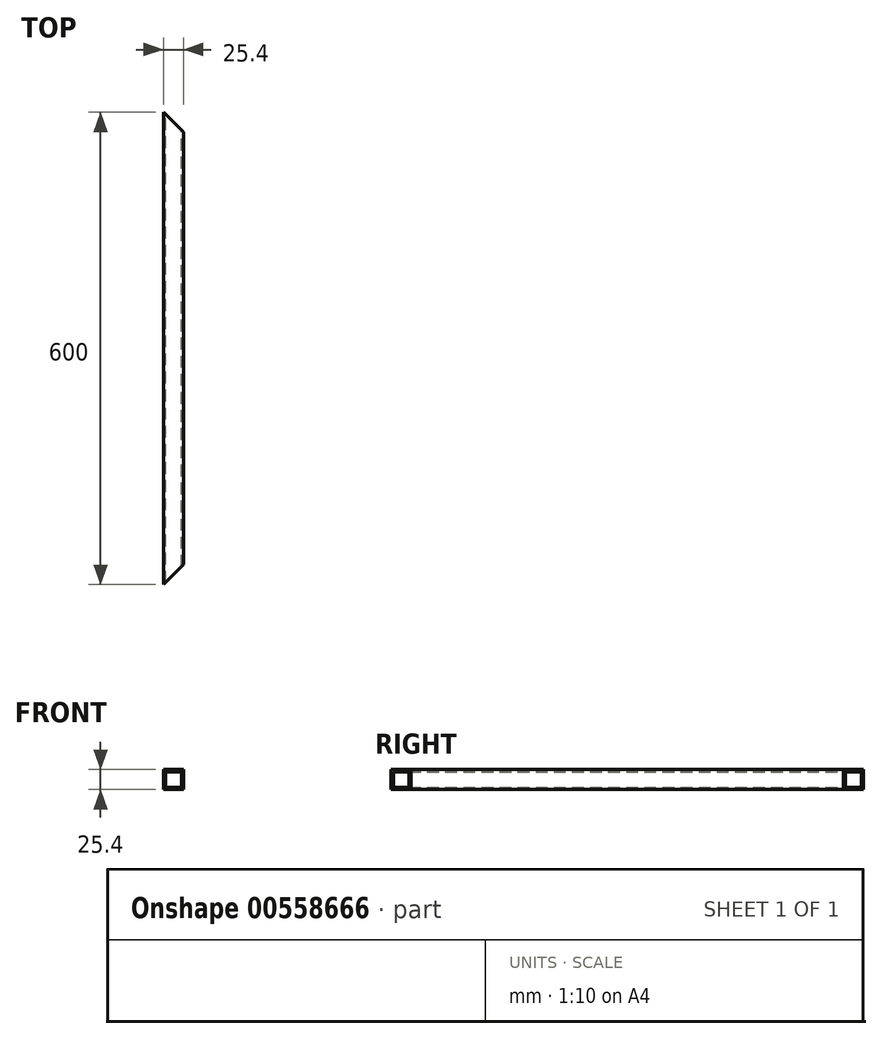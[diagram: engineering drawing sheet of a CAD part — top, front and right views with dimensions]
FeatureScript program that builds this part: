
annotation { "Feature Type Name" : "Feature", "Feature Type Description" : "" }
export const myFeature = defineFeature(function(context is Context, id is Id, definition is map)
    precondition{}
    {
        {
            var Q0;
            Q0=qCreatedBy(makeId("Front.planeOp"),FACE);
            var sketch = newSketch(context, id + "F0", { "sketchPlane" : qUnion([Q0])});
            skLineSegment(sketch, "E0.bottom", {"start": v(-12.7, -12.7) * mm, "end": v(12.7, -12.7) * mm});
            skLineSegment(sketch, "E0.top", {"start": v(-12.7, 12.7) * mm, "end": v(12.7, 12.7) * mm});
            skLineSegment(sketch, "E0.left", {"start": v(-12.7, -12.7) * mm, "end": v(-12.7, 12.7) * mm});
            skLineSegment(sketch, "E0.right", {"start": v(12.7, -12.7) * mm, "end": v(12.7, 12.7) * mm});
            skPoint(sketch, "E0.middle", {"position": v(0, 0) * mm});
            skLineSegment(sketch, "E1.bottom", {"start": v(-10, -10) * mm, "end": v(10, -10) * mm});
            skLineSegment(sketch, "E1.top", {"start": v(-10, 10) * mm, "end": v(10, 10) * mm});
            skLineSegment(sketch, "E1.left", {"start": v(-10, -10) * mm, "end": v(-10, 10) * mm});
            skLineSegment(sketch, "E1.right", {"start": v(10, -10) * mm, "end": v(10, 10) * mm});
            skSolve(sketch);
        }
        {
            var Q0;
            Q0 = qSketchRegion(id + "F0", true);
            extrude(context, id + "F1", {"entities" : qUnion([Q0]), "depth" : 600 * mm, "offsetDistance" : 25 * mm});
        }
        {
            var Q0;
            Q0=makeQuery(id+"F1.opExtrude","SWEPT_FACE",FACE,{"disambiguationData":[OSD([sQuery(id+"F0.wireOp",EDGE,"E0.top")])]});
            var sketch = newSketch(context, id + "F2", { "sketchPlane" : qUnion([Q0])});
            skLineSegment(sketch, "E2", {"start": v(-12.7, 0) * mm, "end": v(12.7, -25.4) * mm});
            skLineSegment(sketch, "E3", {"start": v(-12.7, -600) * mm, "end": v(12.7, -574.6) * mm});
            skSolve(sketch);
        }
        {
            var Q0;
            Q0 = qSketchRegion(id + "F2", true);
            var Q1;
            {var subQ0=sQuery(id+"F2.wireOp",EDGE,"E3");Q1=makeQuery(id+"F2.imprint","IMPRINT",FACE,{"disambiguationData":[TD([[makeQuery(id+"F2.imprint","IMPRINT",EDGE,{"derivedFrom":subQ0}),-1.0]])]});}
            var Q2;
            {var subQ0=sQuery(id+"F2.wireOp",EDGE,"E2");Q2=makeQuery(id+"F2.imprint","IMPRINT",FACE,{"disambiguationData":[TD([[makeQuery(id+"F2.imprint","IMPRINT",EDGE,{"derivedFrom":subQ0}),1.0]])]});}
            extrude(context, id + "F3", {"entities" : qUnion([Q0, Q1, Q2]), "operationType" : NewBodyOperationType.REMOVE, "oppositeDirection" : true, "depth" : 26 * mm, "offsetDistance" : 25 * mm});
        }
    });
